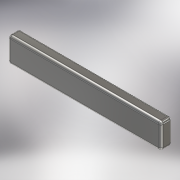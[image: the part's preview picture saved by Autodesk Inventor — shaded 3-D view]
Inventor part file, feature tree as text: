
AUTODESK INVENTOR PART (.ipt)
format: ipt  version: 2018 (Build 220112000, 112)  size: 128,000 bytes
history: native  units: mm
features: extrude x1, fillet x1, sketch x1
ambient origin geometry x8: Origin, YZ Plane, XZ Plane, XY Plane, X Axis, Y Axis, Z Axis, Center Point
bodies: Solid1 (feature_tree)
feature tree (3):
  extrude  "Extrusion1"  Depth=9.5mm
  fillet  "Fillet1"  Radius=4.3mm
  sketch  "Sketch1"  dims[d0=58.0mm d1=9.5mm d2=4.3mm d3=0.0mm d4=1.0mm]
